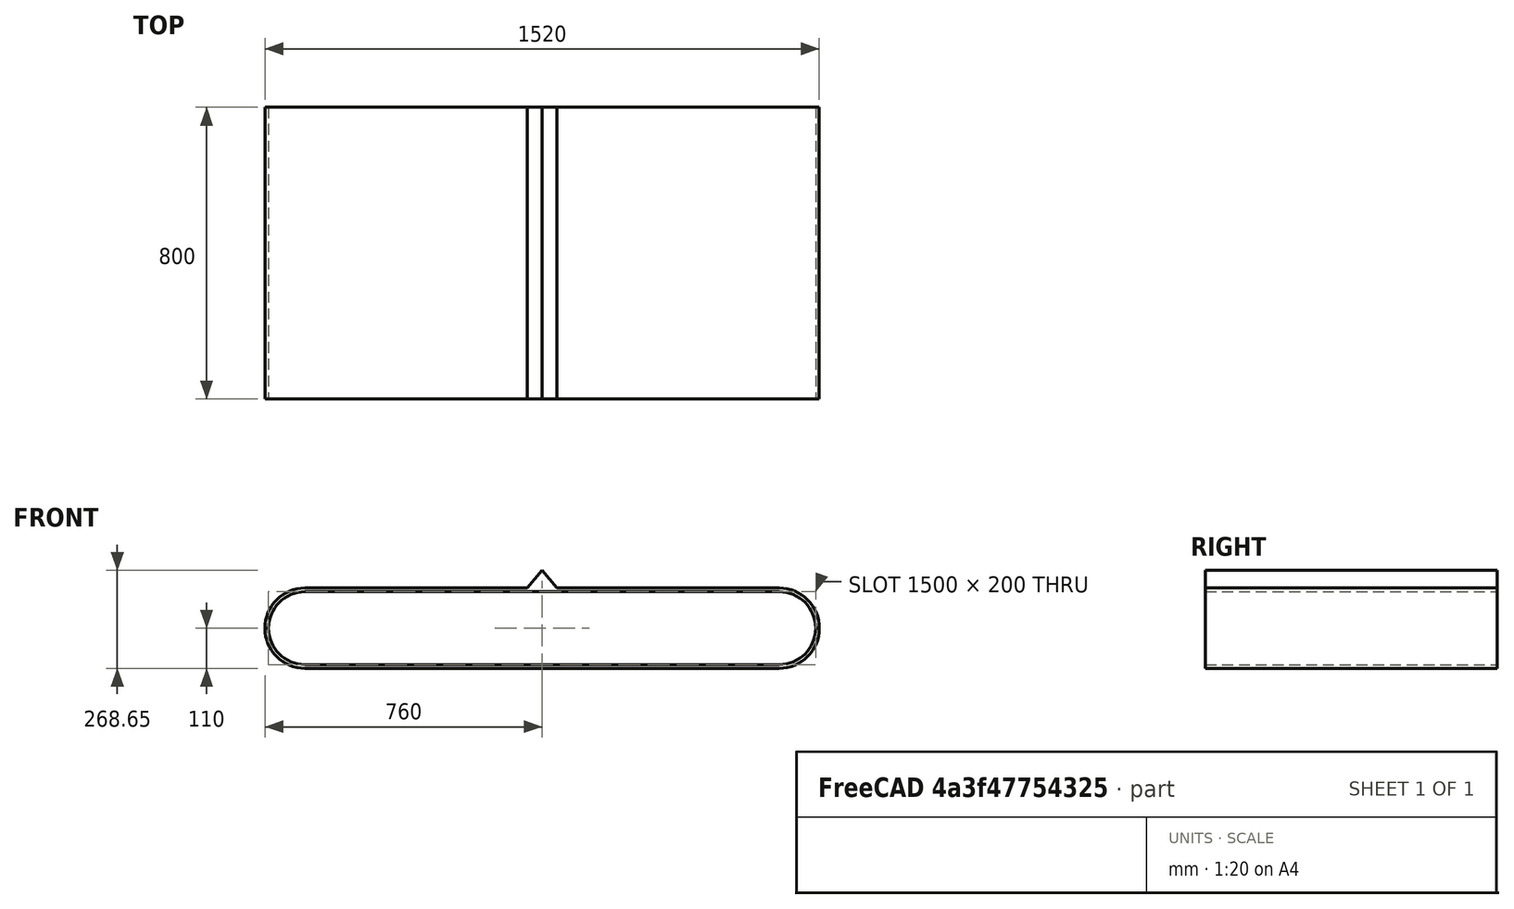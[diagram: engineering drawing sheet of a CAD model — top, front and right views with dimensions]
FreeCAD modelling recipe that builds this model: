
FCSTD DOCUMENT
Label: conveyor_belt2
objects: Sketcher::SketchObject×1, PartDesign::Pad×1
note: 3 computed .brp shape members not serialized (recipe doc carries the construction recipe); baked Part::Feature solids carry a one-line shape summary decoded from their .brp

FEATURE [Sketcher::SketchObject] Sketch
  Placement = pos=(0,-400,0) rot=(1,0,0;1.5708rad)
  sketch-geometry (11):
    g0: LineSegment StartX=-650 StartY=110 StartZ=0 EndX=-40.8209 EndY=110 EndZ=0
    g1: LineSegment StartX=-650 StartY=-110 StartZ=0 EndX=650 EndY=-110 EndZ=0
    g2: ArcOfCircle CenterX=650 CenterY=0 CenterZ=0 NormalX=0 NormalY=0 NormalZ=1 Radius=110 StartAngle=4.71239 EndAngle=7.85398
    g3: ArcOfCircle CenterX=-650 CenterY=0 CenterZ=0 NormalX=0 NormalY=0 NormalZ=1 Radius=110 StartAngle=1.5708 EndAngle=4.71239
    g4: LineSegment StartX=-650 StartY=100 StartZ=0 EndX=650 EndY=100 EndZ=0
    g5: LineSegment StartX=-650 StartY=-100 StartZ=0 EndX=650 EndY=-100 EndZ=0
    g6: ArcOfCircle CenterX=-650 CenterY=0 CenterZ=0 NormalX=0 NormalY=0 NormalZ=1 Radius=100 StartAngle=1.5708 EndAngle=4.71239
    g7: ArcOfCircle CenterX=650 CenterY=0 CenterZ=0 NormalX=0 NormalY=0 NormalZ=1 Radius=100 StartAngle=4.71239 EndAngle=7.85398
    g8: LineSegment StartX=-40.8209 StartY=110 StartZ=0 EndX=0 EndY=158.649 EndZ=0
    g9: LineSegment StartX=0 StartY=158.649 StartZ=0 EndX=40.8209 EndY=110 EndZ=0
    g10: LineSegment StartX=40.8209 StartY=110 StartZ=0 EndX=650 EndY=110 EndZ=0
  constraints (34):
    c: Coincident(g2,g10)
    c: Coincident(g2,g1)
    c: Coincident(g3,g0)
    c: Coincident(g3,g1)
    c: Tangent(g3,g0)
    c: Tangent(g1,g3)
    c: Tangent(g2,g1)
    c: Tangent(g0,g2)
    c: Equal(g3,g2)
    c: Coincident(g6,g3)
    c: Coincident(g6,g4)
    c: Coincident(g6,g5)
    c: Coincident(g7,g2)
    c: Coincident(g7,g4)
    c: Coincident(g7,g5)
    c: Parallel(g5,g1)
    c: Parallel(g0,g4)
    c: Tangent(g4,g6)
    c: Tangent(g4,g7)
    c: Tangent(g6,g5)
    c: Coincident(g9,g8)
    c: Equal(g8,g9)
    c: Angle(g0,g8) = 0.872665
    c: Coincident(g0,g8)
    c: Coincident(g10,g9)
    c: Tangent(g0,g10)
    c: Distance(g8) = 63.5061
    c: DistanceY(g4,g5) = -200
    c: DistanceY(g0,g1) = -220
    c: Horizontal(g10)
    c: DistanceX(g5) = -650
    c: DistanceX(g5) = 650
    c: DistanceY(g4) = 100
    c: DistanceX(g8) = 0
FEATURE [PartDesign::Pad] Pad
  Length = 800
  MirroredExtent = false
  Reversed = true
  Sketch = -> Sketch
